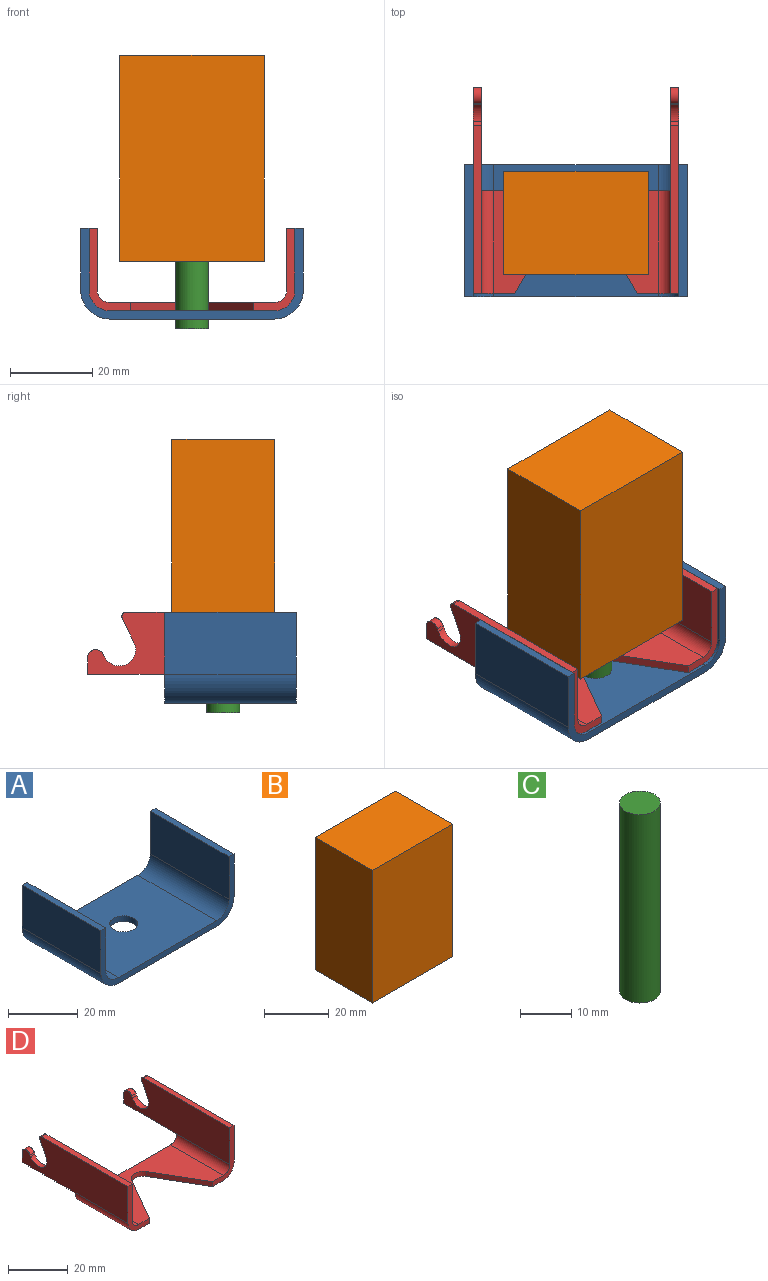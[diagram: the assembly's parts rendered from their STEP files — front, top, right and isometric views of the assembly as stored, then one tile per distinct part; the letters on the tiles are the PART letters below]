
ASSEMBLY  parts=4 mates=2
PART A: 15 faces, bbox 54x32x22 mm
  f0: plane 32x2mm, normal (0,0,1), area 64mm2, adj f1,f11,f12,f13
  f1: plane 32x15mm, normal (-1,0,0), area 480mm2, adj f0,f2,f12,f13
  f2: cylinder r=7mm len=32mm, axis (0,-1,0), area 351.9mm2, adj f1,f3,f12,f13
  f3: plane 40x32mm, normal (0,0,-1), area 1229.7mm2, adj f2,f4,f12,f13,f14
  f4: cylinder r=7mm len=32mm, axis (0,-1,0), area 351.9mm2, adj f3,f5,f12,f13
  f5: plane 32x15mm, normal (1,0,0), area 480mm2, adj f4,f6,f12,f13
  f6: plane 32x2mm, normal (0,0,1), area 64mm2, adj f5,f7,f12,f13
  f7: plane 32x15mm, normal (-1,0,0), area 480mm2, adj f6,f8,f12,f13
  f8: cylinder r=5mm len=32mm, axis (0,-1,0), area 251.3mm2, adj f7,f9,f12,f13
  f9: plane 40x32mm, normal (0,0,1), area 1229.7mm2, adj f8,f10,f12,f13,f14
  f10: cylinder r=5mm len=32mm, axis (0,-1,0), area 251.3mm2, adj f9,f11,f12,f13
  f11: plane 32x15mm, normal (1,0,0), area 480mm2, adj f0,f10,f12,f13
  f12: plane 54x22mm, normal (0,1,0), area 177.7mm2, adj f0,f1,f2,f3,f4,f5,f6,f7
  f13: plane 54x22mm, normal (0,-1,0), area 177.7mm2, adj f0,f1,f2,f3,f4,f5,f6,f7
  f14: cylinder r=4mm len=8mm, axis (0,0,1), area 50.3mm2, adj f3,f9
PART B: 8 faces, bbox 35x25x50 mm
  f0: plane 50x35mm, normal (0,-1,0), area 1750mm2, adj f1,f3,f4,f5
  f1: plane 50x25mm, normal (1,0,0), area 1250mm2, adj f0,f2,f4,f5
  f2: plane 50x35mm, normal (0,1,0), area 1750mm2, adj f1,f3,f4,f5
  f3: plane 50x25mm, normal (-1,0,0), area 1250mm2, adj f0,f2,f4,f5
  f4: plane 35x25mm, normal (0,0,1), area 875mm2, adj f0,f1,f2,f3
  f5: plane 35x25mm, normal (0,0,-1), area 824.7mm2, adj f0,f1,f2,f3,f6
  f6: cylinder r=4mm len=25mm, axis (0,0,1), area 628.3mm2, adj f5,f7
  f7: plane 8x8mm, normal (0,0,-1), area 50.3mm2, adj f6
PART C: 3 faces, bbox 8x8x45 mm
  f0: cylinder r=4mm len=45mm, axis (0,0,1), area 1131mm2, adj f1,f2
  f1: plane 8x8mm, normal (0,0,-1), area 50.3mm2, adj f0
  f2: plane 8x8mm, normal (0,0,1), area 50.3mm2, adj f0
PART D: 32 faces, bbox 50x50x20 mm
  f0: plane 20x10.13mm, normal (0,-1,0), area 52.8mm2, adj f1,f3,f6,f7,f11,f15,f16,f30
  f1: plane 40x25mm, normal (0,0,-1), area 628mm2, adj f0,f2,f10,f11,f12,f17,f30,f31
  f2: cylinder r=4mm len=6.93mm, axis (0,0,1), area 16.8mm2, adj f1,f15,f30,f31
  f3: plane 50x15mm, normal (-1,0,0), area 633.7mm2, adj f0,f7,f8,f11,f18,f20,f21,f22
  f4: plane 50x15mm, normal (1,0,0), area 633.7mm2, adj f9,f12,f13,f17,f19,f25,f26,f27
  f5: plane 50x15mm, normal (-1,0,0), area 633.7mm2, adj f9,f13,f14,f17,f19,f25,f26,f27
  f6: plane 50x15mm, normal (1,0,0), area 633.7mm2, adj f0,f7,f8,f16,f18,f20,f21,f22
  f7: plane 40.68x2mm, normal (0,0,1), area 81.4mm2, adj f0,f3,f6,f24
  f8: plane 3.97x2mm, normal (0,1,0), area 7.9mm2, adj f3,f6,f18,f23
  f9: plane 3.97x2mm, normal (0,1,0), area 7.9mm2, adj f4,f5,f19,f29
  f10: plane 50x5mm, normal (0,1,0), area 105.1mm2, adj f1,f11,f12,f14,f15,f16,f18,f19
  f11: cylinder r=5mm len=25mm, axis (0,1,0), area 196.3mm2, adj f0,f1,f3,f10
  f12: cylinder r=5mm len=25mm, axis (0,1,0), area 196.3mm2, adj f1,f4,f10,f17
  f13: plane 40.68x2mm, normal (0,0,1), area 81.4mm2, adj f4,f5,f17,f28
  f14: cylinder r=3mm len=25mm, axis (0,1,0), area 117.8mm2, adj f5,f10,f15,f17
  f15: plane 40x25mm, normal (0,0,1), area 628mm2, adj f0,f2,f10,f14,f16,f17,f30,f31
  f16: cylinder r=3mm len=25mm, axis (0,1,0), area 117.8mm2, adj f0,f6,f10,f15
  f17: plane 20x10.13mm, normal (0,-1,0), area 52.8mm2, adj f1,f4,f5,f12,f13,f14,f15,f31
  f18: plane 25x2mm, normal (0,0,-1), area 50mm2, adj f3,f6,f8,f10
  f19: plane 25x2mm, normal (0,0,-1), area 50mm2, adj f4,f5,f9,f10
  f20: plane 5.79x2.85mm, normal (0,0.9,-0.44), area 12.9mm2, adj f3,f6,f21,f24
  f21: cylinder r=4mm len=7.59mm, axis (-1,0,0), area 25.1mm2, adj f3,f6,f20,f22
  f22: plane 2x0.62mm, normal (0,-0.9,0.44), area 1.4mm2, adj f3,f6,f21,f23
  f23: cylinder r=2mm len=3.79mm, axis (-1,0,0), area 10.7mm2, adj f3,f6,f8,f22
  f24: cylinder r=1mm len=2mm, axis (-1,0,0), area 4.1mm2, adj f3,f6,f7,f20
  f25: plane 2x0.62mm, normal (0,-0.9,0.44), area 1.4mm2, adj f4,f5,f26,f29
  f26: cylinder r=4mm len=7.59mm, axis (-1,0,0), area 25.1mm2, adj f4,f5,f25,f27
  f27: plane 5.79x2.85mm, normal (0,0.9,-0.44), area 12.9mm2, adj f4,f5,f26,f28
  f28: cylinder r=1mm len=2mm, axis (-1,0,0), area 4.1mm2, adj f4,f5,f13,f27
  f29: cylinder r=2mm len=3.79mm, axis (-1,0,0), area 10.7mm2, adj f4,f5,f9,f25
  f30: plane 19.76x11.41mm, normal (0.87,-0.5,0), area 45.6mm2, adj f0,f1,f2,f15
  f31: plane 19.76x11.41mm, normal (-0.87,-0.5,0), area 45.6mm2, adj f1,f2,f15,f17
PLACE A at identity fixed
PLACE B at identity fixed
PLACE C rot(axis=(1,0,0),180deg) t=(0,-14.49,32.69)mm
PLACE D t=(0,0.73,0)mm
MATE slider C.f0 <-> B.f6  axis (0,0,1) through (0,-7.24,40.69)mm
MATE slider D.f0 <-> A.f13  axis (0,-1,0) through (-25,-24.27,12.5)mm
